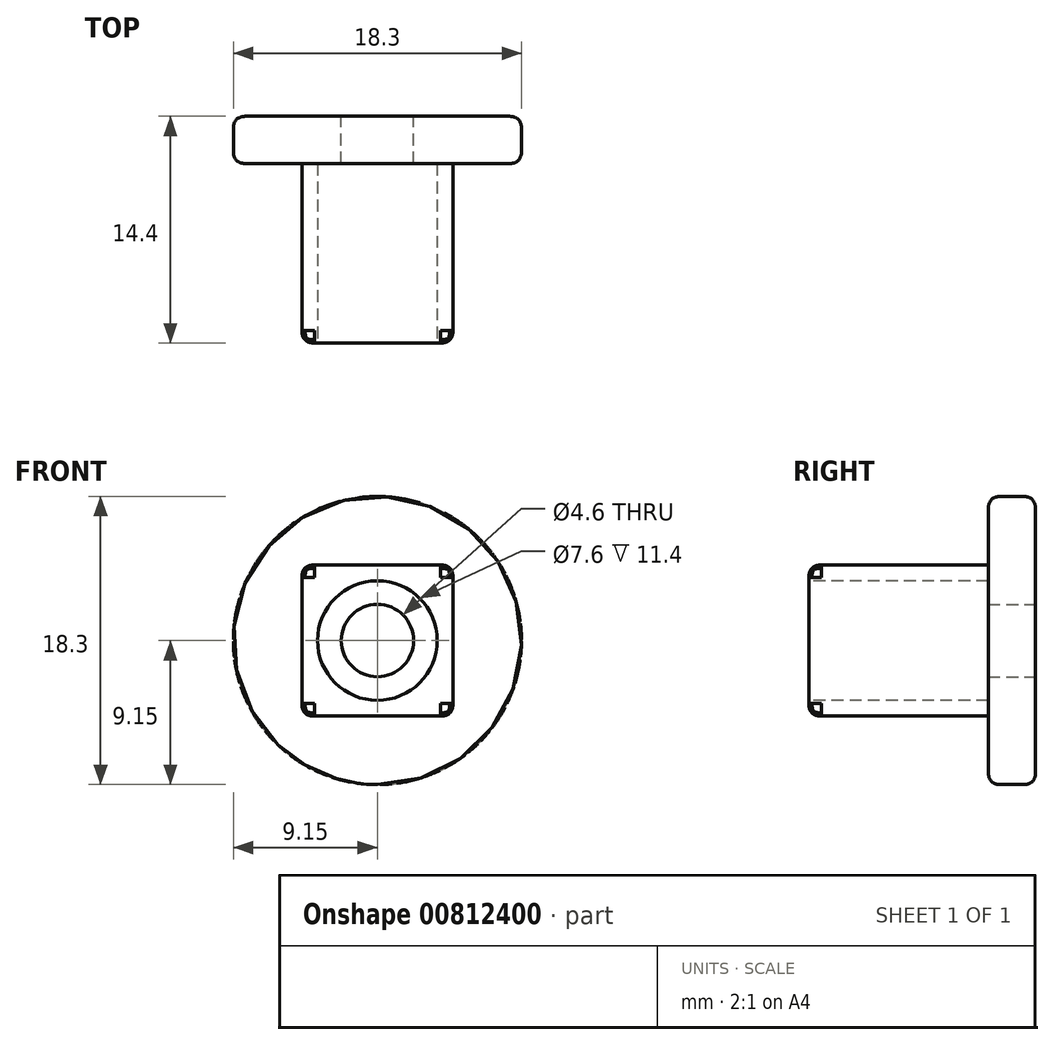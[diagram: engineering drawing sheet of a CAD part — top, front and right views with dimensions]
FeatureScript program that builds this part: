
annotation { "Feature Type Name" : "Feature", "Feature Type Description" : "" }
export const myFeature = defineFeature(function(context is Context, id is Id, definition is map)
    precondition{}
    {
        {
            var Q0;
            Q0=qCreatedBy(makeId("Front.planeOp"),FACE);
            var sketch = newSketch(context, id + "F0", { "sketchPlane" : qUnion([Q0])});
            skCircle(sketch, "E0", {"center": v(0, 0) * mm, "radius": 9.15 * mm});
            skCircle(sketch, "E1", {"center": v(0, 0) * mm, "radius": 2.3 * mm});
            skSolve(sketch);
        }
        {
            var Q0;
            Q0=makeQuery(id+"F0.imprint","IMPRINT",FACE,{"disambiguationData":[TD([[makeQuery(id+"F0.imprint","IMPRINT",EDGE,{"derivedFrom":sQuery(id+"F0.wireOp",EDGE,"E0")}),1.0]])]});
            extrude(context, id + "F1", {"entities" : qUnion([Q0]), "depth" : 3 * mm, "offsetDistance" : 25 * mm});
        }
        {
            var Q0;
            Q0=makeQuery(id+"F1.opExtrude","CAP_FACE",FACE,{"disambiguationData":[OSD([sQuery(id+"F0.wireOp",EDGE,"E0"),sQuery(id+"F0.wireOp",EDGE,"E1")])],"isStart":false});
            var sketch = newSketch(context, id + "F2", { "sketchPlane" : qUnion([Q0])});
            skLineSegment(sketch, "E2.bottom", {"start": v(-4.8, 4.8) * mm, "end": v(4.8, 4.8) * mm});
            skLineSegment(sketch, "E2.top", {"start": v(-4.8, -4.8) * mm, "end": v(4.8, -4.8) * mm});
            skLineSegment(sketch, "E2.left", {"start": v(-4.8, 4.8) * mm, "end": v(-4.8, -4.8) * mm});
            skLineSegment(sketch, "E2.right", {"start": v(4.8, 4.8) * mm, "end": v(4.8, -4.8) * mm});
            skSolve(sketch);
        }
        {
            var Q0;
            Q0=makeQuery(id+"F2.imprint","IMPRINT",FACE,{"disambiguationData":[TD([[makeQuery(id+"F2.imprint","IMPRINT",EDGE,{"derivedFrom":sQuery(id+"F2.wireOp",EDGE,"E2.bottom")}),-1.0]])]});
            extrude(context, id + "F3", {"entities" : qUnion([Q0]), "operationType" : NewBodyOperationType.ADD, "depth" : 11.4 * mm, "offsetDistance" : 25 * mm});
        }
        {
            var Q0;
            Q0=makeQuery(id+"F3.opExtrude","CAP_FACE",FACE,{"disambiguationData":[OSD([sQuery(id+"F0.wireOp",EDGE,"E1"),sQuery(id+"F2.wireOp",EDGE,"E2.bottom"),sQuery(id+"F2.wireOp",EDGE,"E2.top"),sQuery(id+"F2.wireOp",EDGE,"E2.left"),sQuery(id+"F2.wireOp",EDGE,"E2.right")])],"isStart":false});
            var sketch = newSketch(context, id + "F4", { "sketchPlane" : qUnion([Q0])});
            skCircle(sketch, "E3", {"center": v(0, 0) * mm, "radius": 3.8 * mm});
            skSolve(sketch);
        }
        {
            var Q0;
            Q0=makeQuery(id+"F4.imprint","IMPRINT",FACE,{"disambiguationData":[TD([[makeQuery(id+"F4.imprint","IMPRINT",EDGE,{"derivedFrom":sQuery(id+"F4.wireOp",EDGE,"E3")}),1.0]])]});
            extrude(context, id + "F5", {"entities" : qUnion([Q0]), "operationType" : NewBodyOperationType.REMOVE, "oppositeDirection" : true, "depth" : 11.4 * mm, "offsetDistance" : 25 * mm});
        }
        {
            var Q0;
            Q0=makeQuery(id+"F3.opExtrude","CAP_EDGE",EDGE,{"disambiguationData":[OSD([sQuery(id+"F2.wireOp",EDGE,"E2.top")])],"isStart":false});
            var Q1;
            Q1=makeQuery(id+"F3.opExtrude","CAP_EDGE",EDGE,{"disambiguationData":[OSD([sQuery(id+"F2.wireOp",EDGE,"E2.left")])],"isStart":false});
            var Q2;
            Q2=makeQuery(id+"F3.opExtrude","CAP_EDGE",EDGE,{"disambiguationData":[OSD([sQuery(id+"F2.wireOp",EDGE,"E2.bottom")])],"isStart":false});
            var Q3;
            Q3=makeQuery(id+"F3.opExtrude","CAP_EDGE",EDGE,{"disambiguationData":[OSD([sQuery(id+"F2.wireOp",EDGE,"E2.right")])],"isStart":false});
            var Q4;
            Q4=makeQuery(id+"F3.opExtrude","SWEPT_EDGE",EDGE,{"disambiguationData":[OSD([sQuery(id+"F2.wireOp",EDGE,"E2.top"),sQuery(id+"F2.wireOp",EDGE,"E2.right")])]});
            var Q5;
            Q5=makeQuery(id+"F3.opExtrude","SWEPT_EDGE",EDGE,{"disambiguationData":[OSD([sQuery(id+"F2.wireOp",EDGE,"E2.top"),sQuery(id+"F2.wireOp",EDGE,"E2.left")])]});
            var Q6;
            Q6=makeQuery(id+"F3.opExtrude","SWEPT_EDGE",EDGE,{"disambiguationData":[OSD([sQuery(id+"F2.wireOp",EDGE,"E2.bottom"),sQuery(id+"F2.wireOp",EDGE,"E2.right")])]});
            var Q7;
            Q7=makeQuery(id+"F3.opExtrude","SWEPT_EDGE",EDGE,{"disambiguationData":[OSD([sQuery(id+"F2.wireOp",EDGE,"E2.bottom"),sQuery(id+"F2.wireOp",EDGE,"E2.left")])]});
            var Q8;
            Q8=makeQuery(id+"F1.opExtrude","CAP_EDGE",EDGE,{"disambiguationData":[OSD([sQuery(id+"F0.wireOp",EDGE,"E0")])],"isStart":false});
            var Q9;
            Q9=makeQuery(id+"F1.opExtrude","CAP_EDGE",EDGE,{"disambiguationData":[OSD([sQuery(id+"F0.wireOp",EDGE,"E0")])],"isStart":true});
            fillet(context, id + "F6", {"entities" : qUnion([Q0, Q1, Q2, Q3, Q4, Q5, Q6, Q7, Q8, Q9]), "radius" : .8 * mm, "tangentPropagation" : true, "rho" : 0.5, "crossSection" : FilletCrossSection.CONIC, "allowEdgeOverflow" : false});
        }
    });
